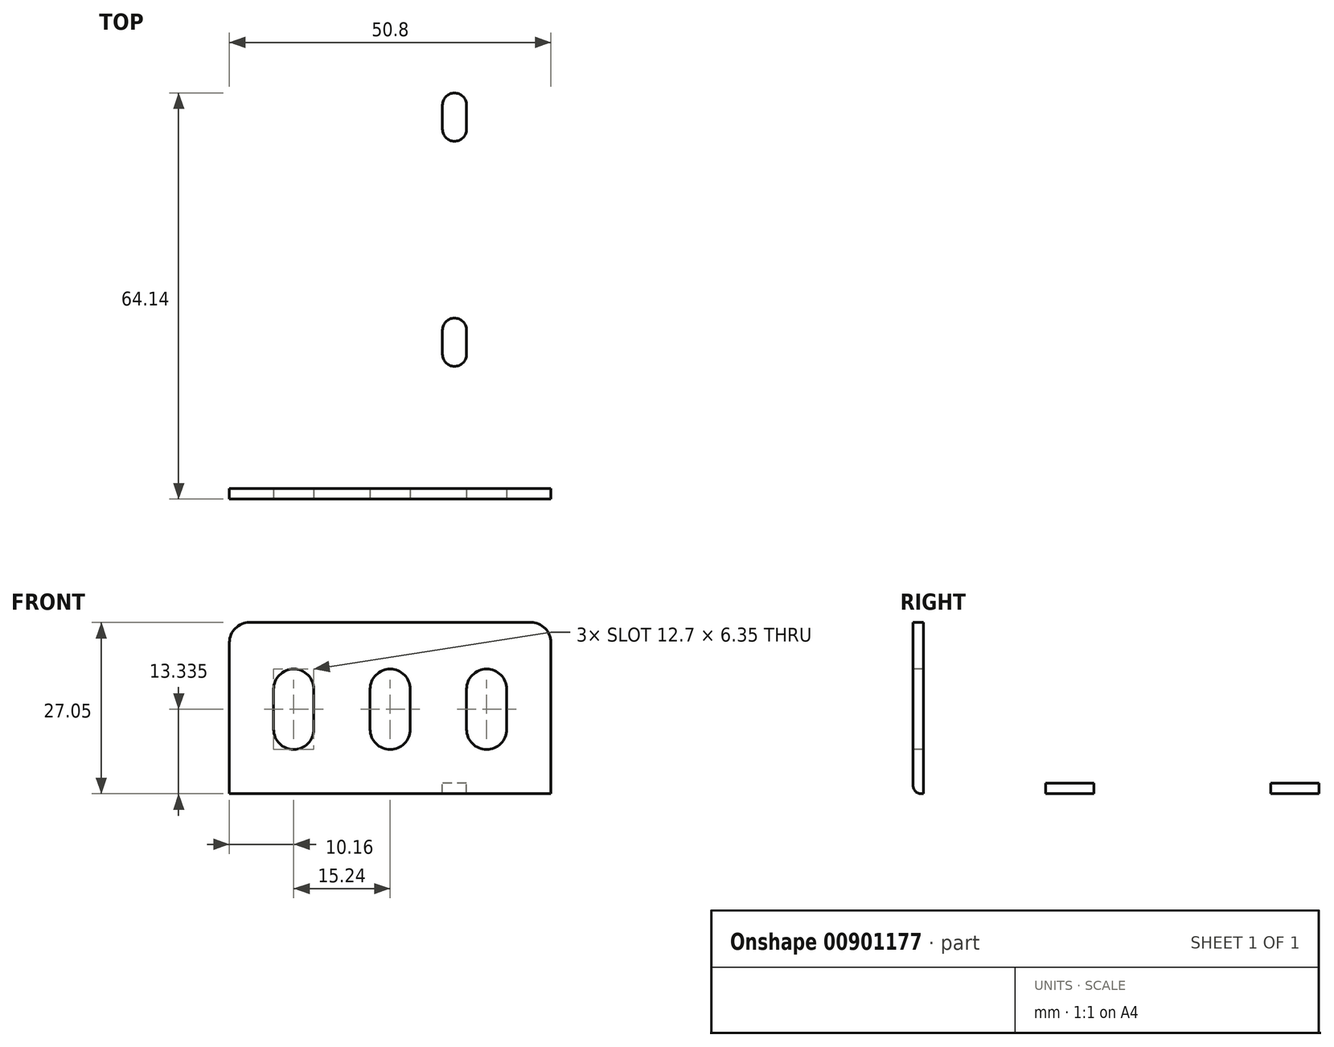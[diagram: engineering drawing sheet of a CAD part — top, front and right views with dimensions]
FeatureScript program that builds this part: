
annotation { "Feature Type Name" : "Feature", "Feature Type Description" : "" }
export const myFeature = defineFeature(function(context is Context, id is Id, definition is map)
    precondition{}
    {
        {
            var Q0;
            Q0=qCreatedBy(makeId("Top.planeOp"),FACE);
            var sketch = newSketch(context, id + "F0", { "sketchPlane" : qUnion([Q0])});
            skLineSegment(sketch, "E0.bottom", {"start": v(-25.4, 34.3) * mm, "end": v(25.4, 34.3) * mm});
            skLineSegment(sketch, "E0.top", {"start": v(-25.4, -41.91) * mm, "end": v(25.4, -41.9) * mm});
            skLineSegment(sketch, "E0.left", {"start": v(-25.4, 34.3) * mm, "end": v(-25.4, -41.91) * mm});
            skLineSegment(sketch, "E0.right", {"start": v(25.4, 34.3) * mm, "end": v(25.4, -41.9) * mm});
            skSolve(sketch);
        }
        {
            var Q0;
            Q0=makeQuery(id+"F0.imprint","IMPRINT",FACE,{"disambiguationData":[TD([[makeQuery(id+"F0.imprint","IMPRINT",EDGE,{"derivedFrom":sQuery(id+"F0.wireOp",EDGE,"E0.bottom")}),-1.0]])]});
            extrude(context, id + "F1", {"entities" : qUnion([Q0]), "depth" : 1.65 * mm, "offsetDistance" : 25.4 * mm});
        }
        {
            var Q0;
            Q0=makeQuery(id+"F1.opExtrude","CAP_FACE",FACE,{"disambiguationData":[OSD([sQuery(id+"F0.wireOp",EDGE,"E0.bottom"),sQuery(id+"F0.wireOp",EDGE,"E0.top"),sQuery(id+"F0.wireOp",EDGE,"E0.left"),sQuery(id+"F0.wireOp",EDGE,"E0.right")])],"isStart":false});
            var sketch = newSketch(context, id + "F2", { "sketchPlane" : qUnion([Q0])});
            skLineSegment(sketch, "E1.bottom", {"start": v(-25.4, -41.91) * mm, "end": v(25.4, -41.91) * mm});
            skLineSegment(sketch, "E1.top", {"start": v(-25.4, -40.26) * mm, "end": v(25.4, -40.26) * mm});
            skLineSegment(sketch, "E1.left", {"start": v(-25.4, -41.91) * mm, "end": v(-25.4, -40.26) * mm});
            skLineSegment(sketch, "E1.right", {"start": v(25.4, -41.91) * mm, "end": v(25.4, -40.26) * mm});
            skSolve(sketch);
        }
        {
            var Q0;
            Q0=makeQuery(id+"F2.imprint","IMPRINT",FACE,{"disambiguationData":[TD([[makeQuery(id+"F2.imprint","IMPRINT",EDGE,{"derivedFrom":sQuery(id+"F2.wireOp",EDGE,"E1.bottom")}),1.0]])]});
            extrude(context, id + "F3", {"entities" : qUnion([Q0]), "operationType" : NewBodyOperationType.ADD, "depth" : 25.4 * mm, "offsetDistance" : 25.4 * mm});
        }
        {
            var Q0;
            Q0=makeQuery(id+"F1.opExtrude","CAP_EDGE",EDGE,{"disambiguationData":[OSD([sQuery(id+"F0.wireOp",EDGE,"E0.top")])],"isStart":true});
            fillet(context, id + "F4", {"entities" : qUnion([Q0]), "radius" : 1.27 * mm, "tangentPropagation" : true, "allowEdgeOverflow" : false});
        }
        {
            var Q0;
            Q0=makeQuery(id+"F1.opExtrude","SWEPT_EDGE",EDGE,{"disambiguationData":[OSD([sQuery(id+"F0.wireOp",EDGE,"E0.bottom"),sQuery(id+"F0.wireOp",EDGE,"E0.right")])]});
            var Q1;
            Q1=makeQuery(id+"F1.opExtrude","SWEPT_EDGE",EDGE,{"disambiguationData":[OSD([sQuery(id+"F0.wireOp",EDGE,"E0.bottom"),sQuery(id+"F0.wireOp",EDGE,"E0.left")])]});
            var Q2;
            Q2=makeQuery(id+"F3.opExtrude","CAP_EDGE",EDGE,{"disambiguationData":[OSD([sQuery(id+"F2.wireOp",EDGE,"E1.right")])],"isStart":false});
            var Q3;
            Q3=makeQuery(id+"F3.opExtrude","CAP_EDGE",EDGE,{"disambiguationData":[OSD([sQuery(id+"F2.wireOp",EDGE,"E1.left")])],"isStart":false});
            fillet(context, id + "F5", {"entities" : qUnion([Q0, Q1, Q2, Q3]), "radius" : 3.17 * mm, "tangentPropagation" : true, "allowEdgeOverflow" : false});
        }
        {
            var Q0;
            Q0=makeQuery(id+"F1.opExtrude","CAP_FACE",FACE,{"disambiguationData":[OSD([sQuery(id+"F0.wireOp",EDGE,"E0.bottom"),sQuery(id+"F0.wireOp",EDGE,"E0.top"),sQuery(id+"F0.wireOp",EDGE,"E0.left"),sQuery(id+"F0.wireOp",EDGE,"E0.right")])],"isStart":false});
            var sketch = newSketch(context, id + "F6", { "sketchPlane" : qUnion([Q0])});
            skPoint(sketch, "E2", {"position": v(-8.89, -1.27) * mm});
            skPoint(sketch, "E3", {"position": v(-8.89, 2.54) * mm});
            skArc(sketch, "E4", {"start": v(-6.98, 2.54) * mm, "mid": v(-8.89, 4.45) * mm, "end": v(-10.8, 2.54) * mm});
            skArc(sketch, "E5", {"start": v(-10.8, -1.27) * mm, "mid": v(-8.89, -3.17) * mm, "end": v(-6.98, -1.27) * mm});
            skLineSegment(sketch, "E6.bottom", {"start": v(-10.8, 2.54) * mm, "end": v(-8.89, 2.54) * mm});
            skLineSegment(sketch, "E6.top", {"start": v(-10.8, -1.27) * mm, "end": v(-8.89, -1.27) * mm});
            skLineSegment(sketch, "E6.left", {"start": v(-10.8, 2.54) * mm, "end": v(-10.8, -1.27) * mm});
            skLineSegment(sketch, "E6.right", {"start": v(-6.98, 2.54) * mm, "end": v(-6.98, -1.27) * mm});
            skLineSegment(sketch, "E7", {"start": v(-8.89, -1.27) * mm, "end": v(-8.89, 2.54) * mm});
            skArc(sketch, "E8.MirrorCS", {"start": v(12.07, 16.51) * mm, "mid": v(10.16, 14.6) * mm, "end": v(8.26, 16.51) * mm});
            skLineSegment(sketch, "E9.MirrorCS", {"start": v(12.07, 20.32) * mm, "end": v(12.07, 16.51) * mm});
            skArc(sketch, "E10.MirrorCS", {"start": v(8.26, 20.32) * mm, "mid": v(10.16, 22.23) * mm, "end": v(12.07, 20.32) * mm});
            skLineSegment(sketch, "E11.MirrorCS", {"start": v(8.26, 20.32) * mm, "end": v(8.26, 16.5) * mm});
            skArc(sketch, "E12.MirrorCS", {"start": v(8.26, -15.24) * mm, "mid": v(10.16, -13.33) * mm, "end": v(12.07, -15.24) * mm});
            skLineSegment(sketch, "E13.MirrorCS", {"start": v(12.06, -15.24) * mm, "end": v(12.06, -19.05) * mm});
            skArc(sketch, "E14.MirrorCS", {"start": v(12.07, -19.05) * mm, "mid": v(10.16, -20.95) * mm, "end": v(8.26, -19.05) * mm});
            skLineSegment(sketch, "E15.MirrorCS", {"start": v(8.26, -15.24) * mm, "end": v(8.26, -19.05) * mm});
            skSolve(sketch);
        }
        {
            var Q0;
            Q0=makeQuery(id+"F6.imprint","IMPRINT",FACE,{"disambiguationData":[TD([[makeQuery(id+"F6.imprint","IMPRINT",EDGE,{"derivedFrom":sQuery(id+"F6.wireOp",EDGE,"5b8b8320-e958-4338-9668-c17e00a209f8")}),1.0]])]});
            var Q1;
            Q1=makeQuery(id+"F6.imprint","IMPRINT",FACE,{"disambiguationData":[TD([[makeQuery(id+"F6.imprint","IMPRINT",EDGE,{"derivedFrom":sQuery(id+"F6.wireOp",EDGE,"E4")}),1.0]])]});
            var Q2;
            Q2=makeQuery(id+"F6.imprint","IMPRINT",FACE,{"disambiguationData":[TD([[makeQuery(id+"F6.imprint","IMPRINT",EDGE,{"derivedFrom":sQuery(id+"F6.wireOp",EDGE,"e72e3b69-3690-4883-b07f-53162f4a673f")}),1.0]])]});
            var Q3;
            Q3=makeQuery(id+"F6.imprint","IMPRINT",FACE,{"disambiguationData":[TD([[makeQuery(id+"F6.imprint","IMPRINT",EDGE,{"derivedFrom":sQuery(id+"F6.wireOp",EDGE,"E6.bottom")}),-1.0]])]});
            var Q4;
            Q4=makeQuery(id+"F6.imprint","IMPRINT",FACE,{"disambiguationData":[TD([[makeQuery(id+"F6.imprint","IMPRINT",EDGE,{"derivedFrom":sQuery(id+"F6.wireOp",EDGE,"E8.MirrorCS")}),-1.0]])]});
            var Q5;
            Q5=makeQuery(id+"F6.imprint","IMPRINT",FACE,{"disambiguationData":[TD([[makeQuery(id+"F6.imprint","IMPRINT",EDGE,{"derivedFrom":sQuery(id+"F6.wireOp",EDGE,"E12.MirrorCS")}),-1.0]])]});
            extrude(context, id + "F7", {"entities" : qUnion([Q0, Q1, Q2, Q3, Q4, Q5]), "operationType" : NewBodyOperationType.REMOVE, "oppositeDirection" : true, "depth" : 25.4 * mm, "offsetDistance" : 25.4 * mm});
        }
        {
            var Q0;
            Q0=makeQuery(id+"F3.boolean.opBoolean","MERGE",FACE,{"derivedFrom":[makeQuery(id+"F1.opExtrude","SWEPT_FACE",FACE,{"disambiguationData":[OSD([sQuery(id+"F0.wireOp",EDGE,"E0.top")])]}),makeQuery(id+"F3.opExtrude","SWEPT_FACE",FACE,{"disambiguationData":[OSD([sQuery(id+"F2.wireOp",EDGE,"E1.bottom")])]})]});
            var sketch = newSketch(context, id + "F8", { "sketchPlane" : qUnion([Q0])});
            skPoint(sketch, "E16", {"position": v(-15.24, 16.51) * mm});
            skPoint(sketch, "E17", {"position": v(-15.24, 10.16) * mm});
            skLineSegment(sketch, "E18.left", {"start": v(-18.41, 16.51) * mm, "end": v(-18.41, 10.16) * mm});
            skLineSegment(sketch, "E18.right", {"start": v(-12.06, 16.51) * mm, "end": v(-12.06, 10.16) * mm});
            skArc(sketch, "E19", {"start": v(-12.06, 16.51) * mm, "mid": v(-15.24, 19.69) * mm, "end": v(-18.41, 16.51) * mm});
            skArc(sketch, "E20", {"start": v(-18.41, 10.16) * mm, "mid": v(-15.24, 6.99) * mm, "end": v(-12.06, 10.16) * mm});
            skPoint(sketch, "E21", {"position": v(0, 10.16) * mm});
            skPoint(sketch, "E22", {"position": v(0, 16.51) * mm});
            skPoint(sketch, "E23", {"position": v(15.24, 16.51) * mm});
            skLineSegment(sketch, "E24.bottom", {"start": v(0, 16.51) * mm, "end": v(3.18, 16.51) * mm});
            skLineSegment(sketch, "E24.top", {"start": v(0, 10.16) * mm, "end": v(3.18, 10.16) * mm});
            skLineSegment(sketch, "E24.right", {"start": v(3.18, 16.51) * mm, "end": v(3.18, 10.16) * mm});
            skLineSegment(sketch, "E25.bottom", {"start": v(15.24, 16.51) * mm, "end": v(18.41, 16.51) * mm});
            skLineSegment(sketch, "E25.right", {"start": v(18.42, 16.51) * mm, "end": v(18.42, 10.16) * mm});
            skArc(sketch, "E26", {"start": v(3.18, 16.51) * mm, "mid": v(0, 19.69) * mm, "end": v(-3.18, 16.51) * mm});
            skArc(sketch, "E27", {"start": v(-3.18, 10.16) * mm, "mid": v(0, 6.99) * mm, "end": v(3.18, 10.16) * mm});
            skArc(sketch, "E28", {"start": v(18.41, 16.51) * mm, "mid": v(15.24, 19.69) * mm, "end": v(12.06, 16.51) * mm});
            skArc(sketch, "E29", {"start": v(12.07, 10.16) * mm, "mid": v(15.24, 6.99) * mm, "end": v(18.41, 10.16) * mm});
            skLineSegment(sketch, "E30.right", {"start": v(-3.18, 16.51) * mm, "end": v(-3.18, 10.16) * mm});
            skLineSegment(sketch, "E31.bottom", {"start": v(18.41, 16.51) * mm, "end": v(15.24, 16.51) * mm});
            skLineSegment(sketch, "E31.top", {"start": v(18.42, 10.16) * mm, "end": v(15.24, 10.16) * mm});
            skLineSegment(sketch, "E31.right", {"start": v(12.06, 16.51) * mm, "end": v(12.06, 10.16) * mm});
            skSolve(sketch);
        }
        {
            var Q0;
            Q0=makeQuery(id+"F8.imprint","IMPRINT",FACE,{"disambiguationData":[TD([[makeQuery(id+"F8.imprint","IMPRINT",EDGE,{"derivedFrom":sQuery(id+"F8.wireOp",EDGE,"E18.left")}),1.0]])]});
            var Q1;
            Q1=makeQuery(id+"F8.imprint","IMPRINT",FACE,{"disambiguationData":[TD([[makeQuery(id+"F8.imprint","IMPRINT",EDGE,{"derivedFrom":sQuery(id+"F8.wireOp",EDGE,"E26")}),1.0]])]});
            var Q2;
            Q2=makeQuery(id+"F8.imprint","IMPRINT",FACE,{"disambiguationData":[TD([[makeQuery(id+"F8.imprint","IMPRINT",EDGE,{"derivedFrom":sQuery(id+"F8.wireOp",EDGE,"E28")}),1.0]])]});
            extrude(context, id + "F9", {"entities" : qUnion([Q0, Q1, Q2]), "operationType" : NewBodyOperationType.REMOVE, "oppositeDirection" : true, "depth" : 25.4 * mm, "offsetDistance" : 25.4 * mm});
        }
    });
